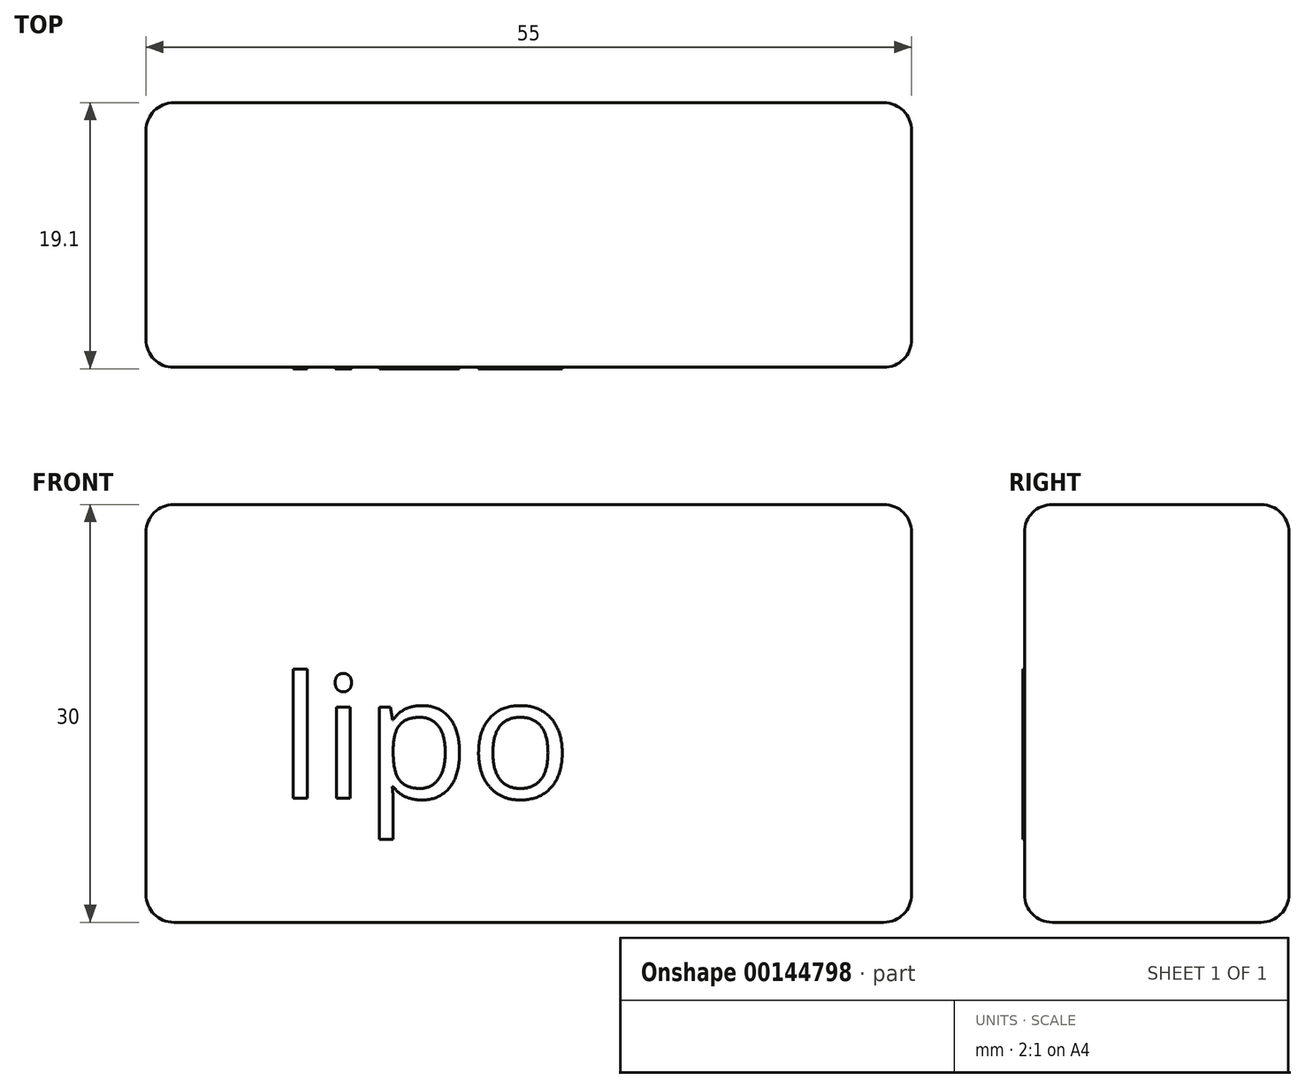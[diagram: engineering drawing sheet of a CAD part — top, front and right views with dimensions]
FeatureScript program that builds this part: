
annotation { "Feature Type Name" : "Feature", "Feature Type Description" : "" }
export const myFeature = defineFeature(function(context is Context, id is Id, definition is map)
    precondition{}
    {
        {
            var Q0;
            Q0=qCreatedBy(makeId("Front.planeOp"),FACE);
            var sketch = newSketch(context, id + "F0", { "sketchPlane" : qUnion([Q0])});
            skLineSegment(sketch, "E0.bottom", {"start": v(-6.61, 2.5) * mm, "end": v(-61.61, 2.5) * mm});
            skLineSegment(sketch, "E0.top", {"start": v(-6.61, 32.5) * mm, "end": v(-61.61, 32.5) * mm});
            skLineSegment(sketch, "E0.left", {"start": v(-6.61, 2.5) * mm, "end": v(-6.61, 32.5) * mm});
            skLineSegment(sketch, "E0.right", {"start": v(-61.61, 2.5) * mm, "end": v(-61.61, 32.5) * mm});
            skPoint(sketch, "E0.middle", {"position": v(-34.11, 17.5) * mm});
            skSolve(sketch);
        }
        {
            var Q0;
            Q0=makeQuery(id+"F0.imprint","IMPRINT",FACE,{"disambiguationData":[TD([[makeQuery(id+"F0.imprint","IMPRINT",EDGE,{"derivedFrom":sQuery(id+"F0.wireOp",EDGE,"E0.bottom")}),-1.0]])]});
            extrude(context, id + "F1", {"entities" : qUnion([Q0]), "depth" : 19 * mm});
        }
        {
            var Q0;
            Q0=makeQuery(id+"F1.opExtrude","SWEPT_EDGE",EDGE,{"disambiguationData":[OSD([sQuery(id+"F0.wireOp",EDGE,"E0.top"),sQuery(id+"F0.wireOp",EDGE,"E0.right")])]});
            var Q1;
            Q1=makeQuery(id+"F1.opExtrude","CAP_EDGE",EDGE,{"disambiguationData":[OSD([sQuery(id+"F0.wireOp",EDGE,"E0.top")])],"isStart":false});
            var Q2;
            Q2=makeQuery(id+"F1.opExtrude","CAP_EDGE",EDGE,{"disambiguationData":[OSD([sQuery(id+"F0.wireOp",EDGE,"E0.right")])],"isStart":false});
            var Q3;
            Q3=makeQuery(id+"F1.opExtrude","CAP_EDGE",EDGE,{"disambiguationData":[OSD([sQuery(id+"F0.wireOp",EDGE,"E0.bottom")])],"isStart":false});
            var Q4;
            Q4=makeQuery(id+"F1.opExtrude","CAP_EDGE",EDGE,{"disambiguationData":[OSD([sQuery(id+"F0.wireOp",EDGE,"E0.left")])],"isStart":false});
            var Q5;
            Q5=makeQuery(id+"F1.opExtrude","CAP_EDGE",EDGE,{"disambiguationData":[OSD([sQuery(id+"F0.wireOp",EDGE,"E0.left")])],"isStart":true});
            var Q6;
            Q6=makeQuery(id+"F1.opExtrude","SWEPT_EDGE",EDGE,{"disambiguationData":[OSD([sQuery(id+"F0.wireOp",EDGE,"E0.top"),sQuery(id+"F0.wireOp",EDGE,"E0.left")])]});
            var Q7;
            Q7=makeQuery(id+"F1.opExtrude","CAP_EDGE",EDGE,{"disambiguationData":[OSD([sQuery(id+"F0.wireOp",EDGE,"E0.top")])],"isStart":true});
            var Q8;
            Q8=makeQuery(id+"F1.opExtrude","SWEPT_EDGE",EDGE,{"disambiguationData":[OSD([sQuery(id+"F0.wireOp",EDGE,"E0.bottom"),sQuery(id+"F0.wireOp",EDGE,"E0.left")])]});
            var Q9;
            Q9=makeQuery(id+"F1.opExtrude","CAP_EDGE",EDGE,{"disambiguationData":[OSD([sQuery(id+"F0.wireOp",EDGE,"E0.bottom")])],"isStart":true});
            var Q10;
            Q10=makeQuery(id+"F1.opExtrude","SWEPT_EDGE",EDGE,{"disambiguationData":[OSD([sQuery(id+"F0.wireOp",EDGE,"E0.bottom"),sQuery(id+"F0.wireOp",EDGE,"E0.right")])]});
            var Q11;
            Q11=makeQuery(id+"F1.opExtrude","CAP_EDGE",EDGE,{"disambiguationData":[OSD([sQuery(id+"F0.wireOp",EDGE,"E0.right")])],"isStart":true});
            fillet(context, id + "F2", {"entities" : qUnion([Q0, Q1, Q2, Q3, Q4, Q5, Q6, Q7, Q8, Q9, Q10, Q11]), "radius" : 2 * mm, "tangentPropagation" : true, "allowEdgeOverflow" : false});
        }
        {
            var Q0;
            Q0=makeQuery(id+"F1.opExtrude","CAP_FACE",FACE,{"disambiguationData":[OSD([sQuery(id+"F0.wireOp",EDGE,"E0.bottom"),sQuery(id+"F0.wireOp",EDGE,"E0.top"),sQuery(id+"F0.wireOp",EDGE,"E0.left"),sQuery(id+"F0.wireOp",EDGE,"E0.right")])],"isStart":false});
            var sketch = newSketch(context, id + "F3", { "sketchPlane" : qUnion([Q0])});
            skText(sketch, "E1", { "text": "lipo", "fontName": "OpenSans-Regular.ttf"});
            const initialGuessF3  = {"E1": [-0.05208, 0.0114, 1, 0, 0.0088]};
            skSetInitialGuess(sketch, initialGuessF3);
            skSolve(sketch);
        }
        {
            var Q0;
            Q0 = qSketchRegion(id + "F3", true);
            extrude(context, id + "F4", {"entities" : qUnion([Q0]), "operationType" : NewBodyOperationType.ADD, "depth" : .1 * mm});
        }
    });
